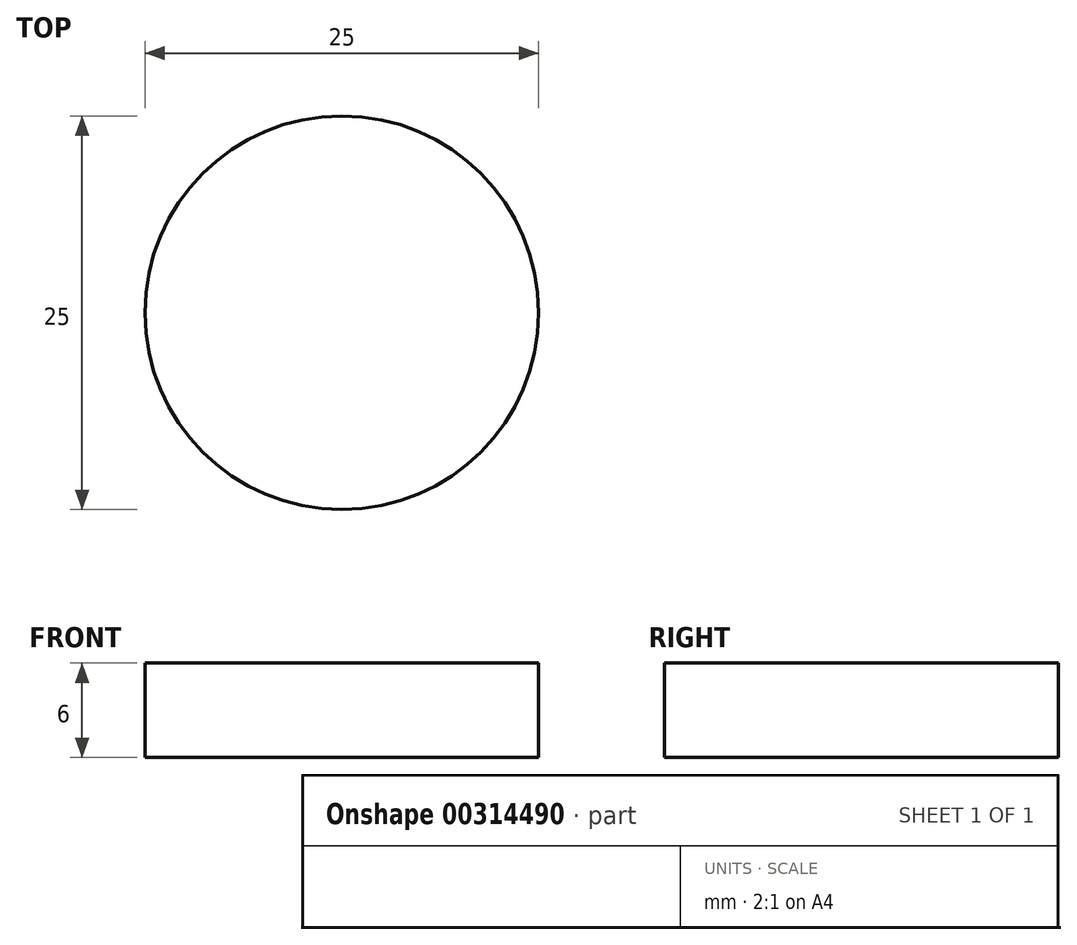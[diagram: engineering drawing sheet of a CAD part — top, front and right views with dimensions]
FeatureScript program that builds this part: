
annotation { "Feature Type Name" : "Feature", "Feature Type Description" : "" }
export const myFeature = defineFeature(function(context is Context, id is Id, definition is map)
    precondition{}
    {
        {
            var Q0;
            Q0=qCreatedBy(makeId("Top.planeOp"),FACE);
            var sketch = newSketch(context, id + "F0", { "sketchPlane" : qUnion([Q0])});
            skCircle(sketch, "E0", {"center": v(-19.25, 0) * mm, "radius": 12.5 * mm});
            skLineSegment(sketch, "E1", {"start": v(-36.35, -14.4) * mm, "end": v(-33.85, -11.9) * mm});
            skLineSegment(sketch, "E2", {"start": v(-34.15, -16.6) * mm, "end": v(-31.65, -14.1) * mm});
            skArc(sketch, "E3", {"start": v(-31.65, -14.1) * mm, "mid": v(-31.65, -11.9) * mm, "end": v(-33.85, -11.9) * mm});
            skArc(sketch, "E4", {"start": v(-36.35, -14.4) * mm, "mid": v(-36.35, -16.6) * mm, "end": v(-34.15, -16.6) * mm});
            skLineSegment(sketch, "E5", {"start": v(-33.85, 11.9) * mm, "end": v(-36.35, 14.4) * mm});
            skLineSegment(sketch, "E6", {"start": v(-31.65, 14.1) * mm, "end": v(-34.15, 16.6) * mm});
            skArc(sketch, "E7", {"start": v(-34.15, 16.6) * mm, "mid": v(-36.35, 16.6) * mm, "end": v(-36.35, 14.4) * mm});
            skArc(sketch, "E8", {"start": v(-33.85, 11.9) * mm, "mid": v(-31.65, 11.9) * mm, "end": v(-31.65, 14.1) * mm});
            skLineSegment(sketch, "E9", {"start": v(-5.35, -16.6) * mm, "end": v(-7.85, -14.1) * mm});
            skLineSegment(sketch, "E10", {"start": v(-3.15, -14.4) * mm, "end": v(-5.65, -11.9) * mm});
            skArc(sketch, "E11", {"start": v(-5.65, -11.9) * mm, "mid": v(-7.85, -11.9) * mm, "end": v(-7.85, -14.1) * mm});
            skArc(sketch, "E12", {"start": v(-5.35, -16.6) * mm, "mid": v(-3.15, -16.6) * mm, "end": v(-3.15, -14.4) * mm});
            skLineSegment(sketch, "E13", {"start": v(-3.15, 14.4) * mm, "end": v(-5.65, 11.9) * mm});
            skLineSegment(sketch, "E14", {"start": v(-5.35, 16.6) * mm, "end": v(-7.85, 14.1) * mm});
            skArc(sketch, "E15", {"start": v(-7.85, 14.1) * mm, "mid": v(-7.85, 11.9) * mm, "end": v(-5.65, 11.9) * mm});
            skArc(sketch, "E16", {"start": v(-3.15, 14.4) * mm, "mid": v(-3.15, 16.6) * mm, "end": v(-5.35, 16.6) * mm});
            skCircle(sketch, "E17", {"center": v(12.8, 10) * mm, "radius": 2.55 * mm});
            skCircle(sketch, "E18", {"center": v(32.8, 10) * mm, "radius": 2.55 * mm});
            skCircle(sketch, "E19", {"center": v(32.8, 0) * mm, "radius": 2.55 * mm});
            skCircle(sketch, "E20", {"center": v(12.8, 0) * mm, "radius": 2.55 * mm});
            skCircle(sketch, "E21", {"center": v(12.8, -10) * mm, "radius": 2.55 * mm});
            skCircle(sketch, "E22", {"center": v(32.8, -10) * mm, "radius": 2.55 * mm});
            skArc(sketch, "E23", {"start": v(-38, 19.75) * mm, "mid": v(-40.12, 18.87) * mm, "end": v(-41, 16.75) * mm});
            skLineSegment(sketch, "E24", {"start": v(-41, -16.75) * mm, "end": v(-41, 16.75) * mm});
            skArc(sketch, "E25", {"start": v(-41, -16.75) * mm, "mid": v(-40.12, -18.87) * mm, "end": v(-38, -19.75) * mm});
            skLineSegment(sketch, "E26", {"start": v(38, -19.75) * mm, "end": v(-38, -19.75) * mm});
            skArc(sketch, "E27", {"start": v(38, -19.75) * mm, "mid": v(40.12, -18.87) * mm, "end": v(41, -16.75) * mm});
            skLineSegment(sketch, "E28", {"start": v(41, 16.75) * mm, "end": v(41, -16.75) * mm});
            skLineSegment(sketch, "E29", {"start": v(38, 19.75) * mm, "end": v(-38, 19.75) * mm});
            skArc(sketch, "E30", {"start": v(41, 16.75) * mm, "mid": v(40.12, 18.87) * mm, "end": v(38, 19.75) * mm});
            skCircle(sketch, "E31", {"center": v(31.4, -16.75) * mm, "radius": 1.3 * mm});
            skSolve(sketch);
        }
        {
            var Q0;
            Q0=makeQuery(id+"F0.imprint","IMPRINT",FACE,{"disambiguationData":[TD([[makeQuery(id+"F0.imprint","IMPRINT",EDGE,{"derivedFrom":sQuery(id+"F0.wireOp",EDGE,"E0")}),1.0]])]});
            extrude(context, id + "F1", {"entities" : qUnion([Q0]), "depth" : 6 * mm});
        }
    });
